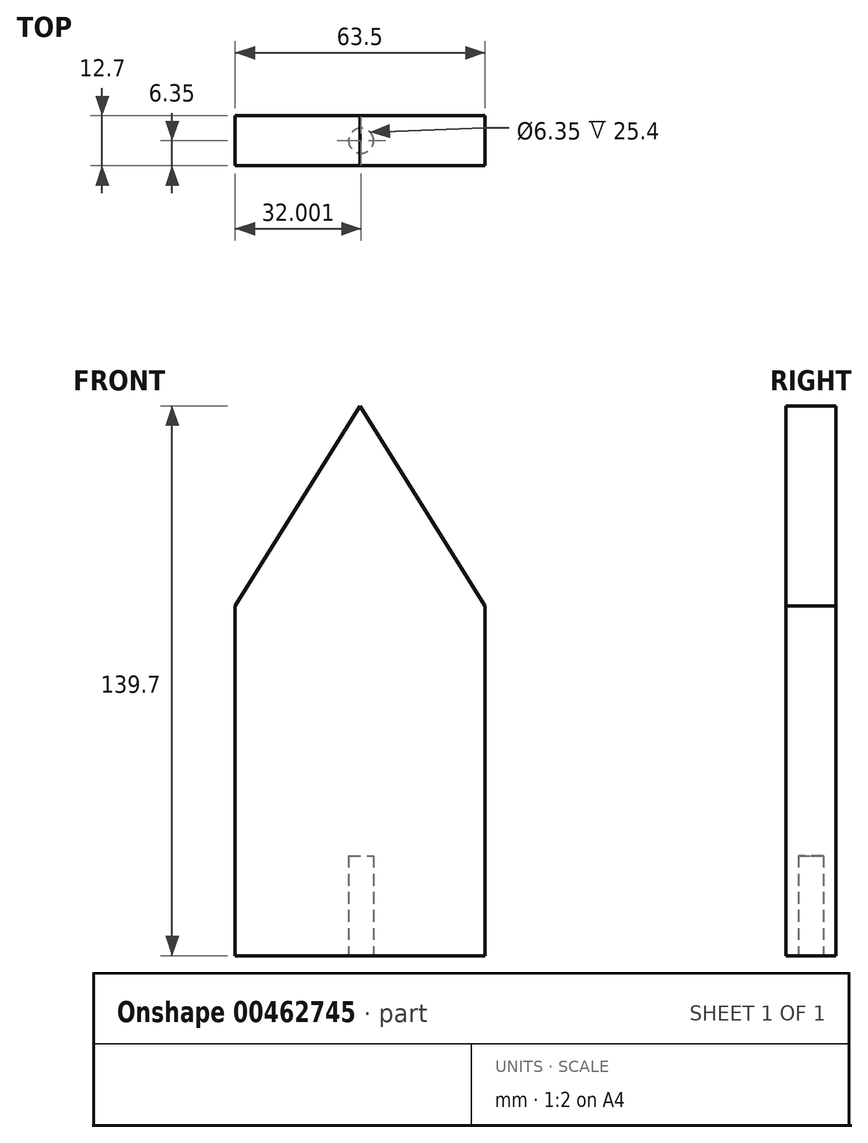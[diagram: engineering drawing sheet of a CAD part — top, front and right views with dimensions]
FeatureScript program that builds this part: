
annotation { "Feature Type Name" : "Feature", "Feature Type Description" : "" }
export const myFeature = defineFeature(function(context is Context, id is Id, definition is map)
    precondition{}
    {
        {
            var Q0;
            Q0=qCreatedBy(makeId("Front.planeOp"),FACE);
            var sketch = newSketch(context, id + "F0", { "sketchPlane" : qUnion([Q0])});
            skLineSegment(sketch, "E0.bottom", {"start": v(-51.81, 91.2) * mm, "end": v(11.69, 91.2) * mm});
            skLineSegment(sketch, "E0.top", {"start": v(-51.81, -48.5) * mm, "end": v(11.69, -48.5) * mm});
            skLineSegment(sketch, "E0.left", {"start": v(-51.81, 91.2) * mm, "end": v(-51.81, -48.5) * mm});
            skLineSegment(sketch, "E0.right", {"start": v(11.69, 91.2) * mm, "end": v(11.69, -48.5) * mm});
            skSolve(sketch);
        }
        {
            var Q0;
            Q0 = qSketchRegion(id + "F0", true);
            extrude(context, id + "F1", {"entities" : qUnion([Q0]), "depth" : 12.7 * mm});
        }
        {
            var Q0;
            Q0=makeQuery(id+"F1.opExtrude","CAP_FACE",FACE,{"disambiguationData":[OSD([sQuery(id+"F0.wireOp",EDGE,"E0.bottom"),sQuery(id+"F0.wireOp",EDGE,"E0.top"),sQuery(id+"F0.wireOp",EDGE,"E0.left"),sQuery(id+"F0.wireOp",EDGE,"E0.right")])],"isStart":false});
            var sketch = newSketch(context, id + "F2", { "sketchPlane" : qUnion([Q0])});
            skLineSegment(sketch, "E1", {"start": v(-20.06, 91.2) * mm, "end": v(11.69, 40.4) * mm});
            skLineSegment(sketch, "E2", {"start": v(11.69, 40.4) * mm, "end": v(11.69, 91.2) * mm});
            skLineSegment(sketch, "E3", {"start": v(11.69, 91.2) * mm, "end": v(-20.06, 91.2) * mm});
            skLineSegment(sketch, "E4", {"start": v(-51.81, 40.4) * mm, "end": v(-51.81, 91.2) * mm});
            skLineSegment(sketch, "E5", {"start": v(-51.81, 91.2) * mm, "end": v(-20.06, 91.2) * mm});
            skLineSegment(sketch, "E6", {"start": v(-51.81, 40.4) * mm, "end": v(-20.06, 91.2) * mm});
            skSolve(sketch);
        }
        {
            var Q0;
            Q0=makeQuery(id+"F2.imprint","IMPRINT",FACE,{"disambiguationData":[TD([[makeQuery(id+"F2.imprint","IMPRINT",EDGE,{"derivedFrom":sQuery(id+"F2.wireOp",EDGE,"E4")}),1.0]])]});
            var Q1;
            Q1=makeQuery(id+"F2.imprint","IMPRINT",FACE,{"disambiguationData":[TD([[makeQuery(id+"F2.imprint","IMPRINT",EDGE,{"derivedFrom":sQuery(id+"F2.wireOp",EDGE,"E1")}),1.0]])]});
            extrude(context, id + "F3", {"entities" : qUnion([Q0, Q1]), "operationType" : NewBodyOperationType.REMOVE, "oppositeDirection" : true, "depth" : 25.4 * mm});
        }
        {
            var Q0;
            Q0=makeQuery(id+"F1.opExtrude","SWEPT_FACE",FACE,{"disambiguationData":[OSD([sQuery(id+"F0.wireOp",EDGE,"E0.top")])]});
            var sketch = newSketch(context, id + "F4", { "sketchPlane" : qUnion([Q0])});
            skCircle(sketch, "E7", {"center": v(-19.8, 6.35) * mm, "radius": 3.18 * mm});
            skPoint(sketch, "E7.centerSnap0", {"position": v(-51.81, 6.35) * mm});
            skSolve(sketch);
        }
        {
            var Q0;
            Q0=makeQuery(id+"F4.imprint","IMPRINT",FACE,{"disambiguationData":[TD([[makeQuery(id+"F4.imprint","IMPRINT",EDGE,{"derivedFrom":sQuery(id+"F4.wireOp",EDGE,"E7")}),1.0]])]});
            extrude(context, id + "F5", {"entities" : qUnion([Q0]), "operationType" : NewBodyOperationType.REMOVE, "oppositeDirection" : true, "depth" : 25.4 * mm});
        }
    });
